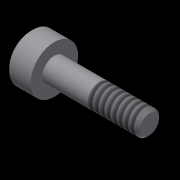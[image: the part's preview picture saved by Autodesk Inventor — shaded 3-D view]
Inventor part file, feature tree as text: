
AUTODESK INVENTOR PART (.ipt)
format: ipt  version: 2020 (Build 240168000, 168)  size: 110,080 bytes
history: native  units: in
note: dims shown in document units (in); Inventor stores cm internally (conversion verified against a paired STEP export)
features: chamfer x2, other x1, revolve x1, thread x1, extrude x1
ambient origin geometry x8: Origin, YZ Plane, XZ Plane, XY Plane, X Axis, Y Axis, Z Axis, Center Point
bodies: Body1 (feature_tree)
feature tree (6):
  other  "實體1"
  revolve  "Revolution1"  [1 undecoded]
  chamfer  "Chamfer5"  Distance=0.0197in
  thread  "Thread8"  [1 undecoded]
  chamfer  "Chamfer6"  Angle=90.0deg  [1 undecoded]
  extrude  "Extrusion18"  Depth=0.0394in
note: 3 required parameter values undecoded (feature->parameter linkage not recoverable at this tier; creation-order binding heuristic only, values carry confidence <= 0.55)